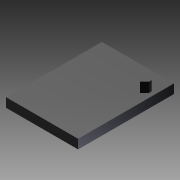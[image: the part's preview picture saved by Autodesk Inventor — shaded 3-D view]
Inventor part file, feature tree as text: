
AUTODESK INVENTOR PART (.ipt)
format: ipt  version: 2011 SP1 (Build 150282100, 282)  size: 91,136 bytes
history: native  units: in
note: dims shown in document units (in); Inventor stores cm internally (conversion verified against a paired STEP export)
features: other x28, extrude x2, sketch x2
ambient origin geometry x8: Origin, YZ Plane, XZ Plane, XY Plane, X Axis, Y Axis, Z Axis, Center Point
bodies: Solid1 (feature_tree)
feature tree (32):
  extrude  "Extrusion1"  Depth=0.032in TaperAngle=0.0deg
  extrude  "Extrusion2"  [1 undecoded]
  other  "cp_body_raiv_XY"
  other  "cp_body_raiv_YZ"
  other  "cp_body_raiv_ZX"
  other  "cp_body_raiv_X"
  other  "cp_body_raiv_Y"
  other  "cp_body_raiv_Z"
  other  "cp_body_raiv_Center"
  other  "cp_body_str_XY"
  other  "cp_body_str_YZ"
  other  "cp_body_str_ZX"
  other  "cp_body_str_X"
  other  "cp_body_str_Y"
  other  "cp_body_str_Z"
  other  "cp_body_str_Center"
  other  "cp_body_togg_rv_XY"
  other  "cp_body_togg_rv_YZ"
  other  "cp_body_togg_rv_ZX"
  other  "cp_body_togg_rv_X"
  other  "cp_body_togg_rv_Y"
  other  "cp_body_togg_rv_Z"
  other  "cp_body_togg_rv_Center"
  other  "cp_body_togstr_XY"
  other  "cp_body_togstr_YZ"
  other  "cp_body_togstr_ZX"
  other  "cp_body_togstr_X"
  other  "cp_body_togstr_Y"
  other  "cp_body_togstr_Z"
  other  "cp_body_togstr_Center"
  sketch  "Sketch_1"  dims[d0=0.03in d1=0.0in d2=0.032in d3=0.0in]
  sketch  "Sketch_11"
note: 1 required parameter value undecoded (feature->parameter linkage not recoverable at this tier; creation-order binding heuristic only, values carry confidence <= 0.55)
